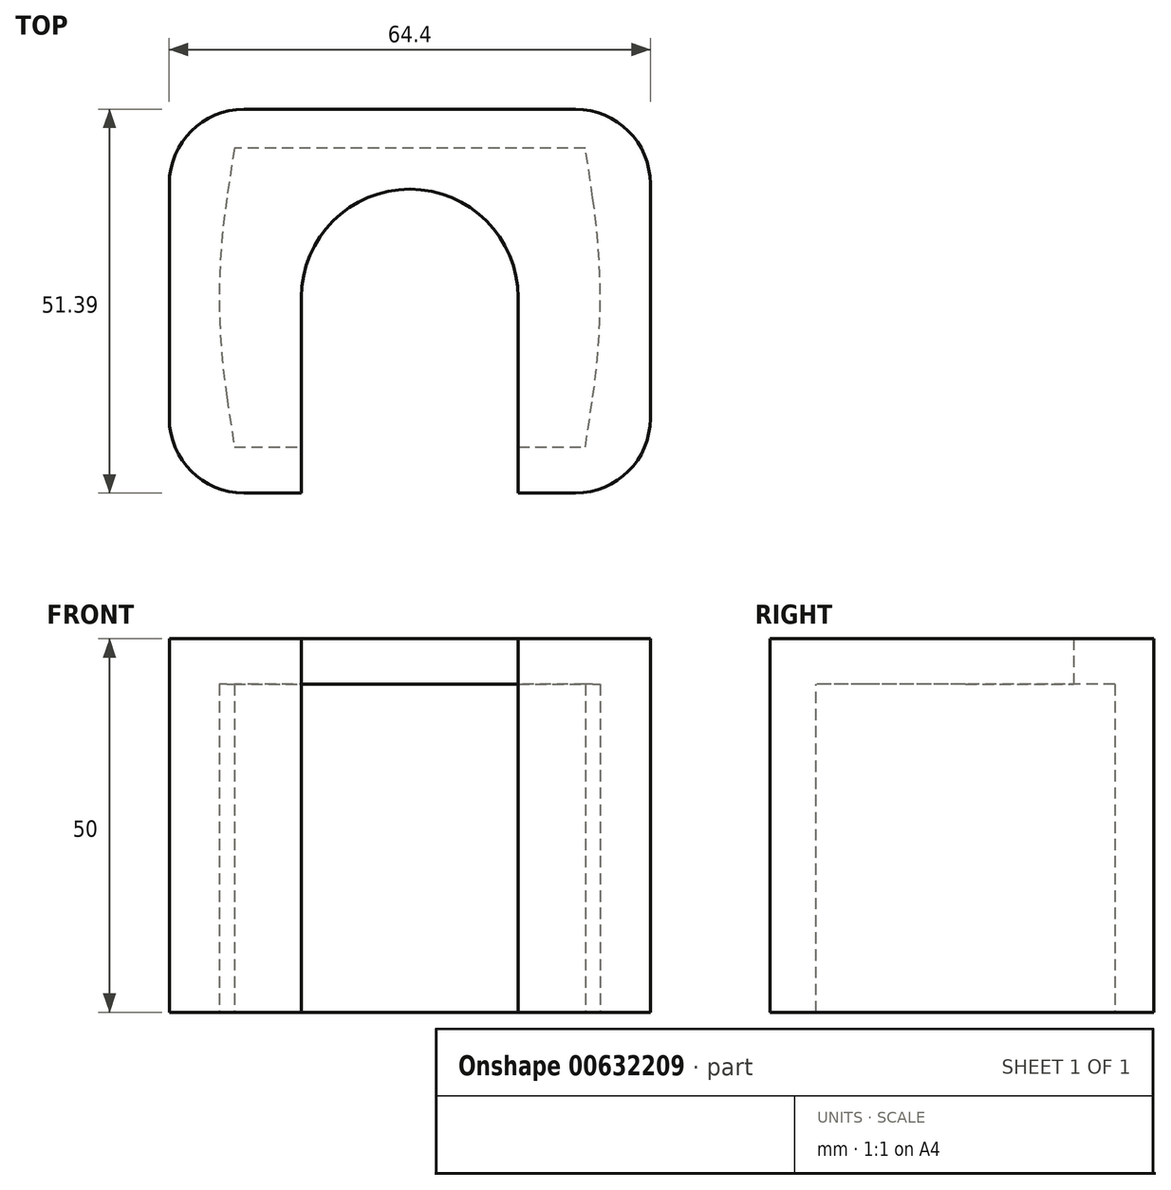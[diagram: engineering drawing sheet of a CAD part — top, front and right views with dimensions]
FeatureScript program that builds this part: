
annotation { "Feature Type Name" : "Feature", "Feature Type Description" : "" }
export const myFeature = defineFeature(function(context is Context, id is Id, definition is map)
    precondition{}
    {
        {
            var Q0;
            Q0=qCreatedBy(makeId("Top.planeOp"),FACE);
            var sketch = newSketch(context, id + "F0", { "sketchPlane" : qUnion([Q0])});
            skPoint(sketch, "E0", {"position": v(-23.5, 20) * mm});
            skPoint(sketch, "E1", {"position": v(23.5, 20) * mm});
            skPoint(sketch, "E2", {"position": v(26.5, 0) * mm});
            skPoint(sketch, "E3", {"position": v(23.5, -20) * mm});
            skPoint(sketch, "E4", {"position": v(-23.5, -20) * mm});
            skPoint(sketch, "E5", {"position": v(-26.5, 0) * mm});
            skLineSegment(sketch, "E6", {"start": v(-23.5, 20) * mm, "end": v(-24.5, 13.35) * mm});
            skLineSegment(sketch, "E7", {"start": v(-24.5, -13.35) * mm, "end": v(-23.5, -20) * mm});
            skLineSegment(sketch, "E8", {"start": v(-23.5, -20) * mm, "end": v(23.5, -20) * mm});
            skLineSegment(sketch, "E9", {"start": v(23.5, -20) * mm, "end": v(24.5, -13.35) * mm});
            skLineSegment(sketch, "E10", {"start": v(24.5, 13.35) * mm, "end": v(23.5, 20) * mm});
            skLineSegment(sketch, "E11", {"start": v(23.5, 20) * mm, "end": v(-23.5, 20) * mm});
            skArc(sketch, "E12.filletArc", {"start": v(-24.5, 13.35) * mm, "mid": v(-25.5, 0) * mm, "end": v(-24.5, -13.35) * mm});
            skPoint(sketch, "E13", {"position": v(-23.5, 0) * mm});
            skArc(sketch, "E14.filletArc", {"start": v(24.5, -13.35) * mm, "mid": v(25.5, 0) * mm, "end": v(24.5, 13.35) * mm});
            skSolve(sketch);
        }
        {
            var Q0;
            Q0=qCreatedBy(makeId("Top.planeOp"),FACE);
            var sketch = newSketch(context, id + "F1", { "sketchPlane" : qUnion([Q0])});
            skLineSegment(sketch, "E15.bottom", {"start": v(22.2, 25.2) * mm, "end": v(-22.2, 25.2) * mm});
            skLineSegment(sketch, "E15.top", {"start": v(22.2, -26.18) * mm, "end": v(-22.2, -26.18) * mm});
            skLineSegment(sketch, "E15.left", {"start": v(32.2, 15.2) * mm, "end": v(32.2, -16.18) * mm});
            skLineSegment(sketch, "E15.right", {"start": v(-32.2, 15.2) * mm, "end": v(-32.2, -16.18) * mm});
            skPoint(sketch, "E15.middle", {"position": v(0, 0) * mm});
            skPoint(sketch, "E16.visualSharp", {"position": v(-32.2, 25.2) * mm});
            skArc(sketch, "E16.filletArc", {"start": v(-22.2, 25.2) * mm, "mid": v(-29.27, 22.28) * mm, "end": v(-32.2, 15.2) * mm});
            skPoint(sketch, "E17.visualSharp", {"position": v(32.2, 25.2) * mm});
            skArc(sketch, "E17.filletArc", {"start": v(32.2, 15.2) * mm, "mid": v(29.27, 22.28) * mm, "end": v(22.2, 25.2) * mm});
            skPoint(sketch, "E18.visualSharp", {"position": v(32.2, -26.18) * mm});
            skArc(sketch, "E18.filletArc", {"start": v(22.2, -26.18) * mm, "mid": v(29.27, -23.25) * mm, "end": v(32.2, -16.18) * mm});
            skPoint(sketch, "E19.visualSharp", {"position": v(-32.2, -26.18) * mm});
            skArc(sketch, "E19.filletArc", {"start": v(-32.2, -16.18) * mm, "mid": v(-29.27, -23.25) * mm, "end": v(-22.2, -26.18) * mm});
            skSolve(sketch);
        }
        {
            var Q0;
            Q0=qCreatedBy(makeId("Top.planeOp"),FACE);
            var sketch = newSketch(context, id + "F2", { "sketchPlane" : qUnion([Q0])});
            skCircle(sketch, "E20", {"center": v(0, 0) * mm, "radius": 14.5 * mm});
            skSolve(sketch);
        }
        {
            var Q0;
            Q0 = qSketchRegion(id + "F1", true);
            extrude(context, id + "F3", {"entities" : qUnion([Q0]), "depth" : 50 * mm, "offsetDistance" : 25 * mm});
        }
        {
            var Q0;
            Q0 = qSketchRegion(id + "F2", true);
            extrude(context, id + "F4", {"entities" : qUnion([Q0]), "operationType" : NewBodyOperationType.REMOVE, "depth" : 75 * mm, "offsetDistance" : 25 * mm});
        }
        {
            var Q0;
            Q0 = qSketchRegion(id + "F0", true);
            extrude(context, id + "F5", {"entities" : qUnion([Q0]), "operationType" : NewBodyOperationType.REMOVE, "depth" : 43.9 * mm, "offsetDistance" : 25 * mm});
        }
        {
            var Q0;
            Q0=makeQuery(id+"F3.opExtrude","CAP_FACE",FACE,{"disambiguationData":[OSD([sQuery(id+"F1.wireOp",EDGE,"E15.bottom"),sQuery(id+"F1.wireOp",EDGE,"E15.top"),sQuery(id+"F1.wireOp",EDGE,"E15.left"),sQuery(id+"F1.wireOp",EDGE,"E15.right"),sQuery(id+"F1.wireOp",EDGE,"E16.filletArc"),sQuery(id+"F1.wireOp",EDGE,"E17.filletArc"),sQuery(id+"F1.wireOp",EDGE,"E18.filletArc"),sQuery(id+"F1.wireOp",EDGE,"E19.filletArc")])],"isStart":false});
            var sketch = newSketch(context, id + "F6", { "sketchPlane" : qUnion([Q0])});
            skLineSegment(sketch, "E21.bottom", {"start": v(14.5, 0) * mm, "end": v(-14.5, 0) * mm});
            skLineSegment(sketch, "E21.top", {"start": v(14.5, -29) * mm, "end": v(-14.5, -29) * mm});
            skLineSegment(sketch, "E21.left", {"start": v(14.5, 0) * mm, "end": v(14.5, -29) * mm});
            skLineSegment(sketch, "E21.right", {"start": v(-14.5, 0) * mm, "end": v(-14.5, -29) * mm});
            skPoint(sketch, "E21.middle", {"position": v(0, -14.5) * mm});
            skSolve(sketch);
        }
        {
            var Q0;
            Q0 = qSketchRegion(id + "F6", true);
            extrude(context, id + "F7", {"entities" : qUnion([Q0]), "operationType" : NewBodyOperationType.REMOVE, "oppositeDirection" : true, "depth" : 59.8 * mm, "offsetDistance" : 25 * mm});
        }
    });
